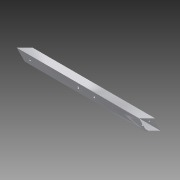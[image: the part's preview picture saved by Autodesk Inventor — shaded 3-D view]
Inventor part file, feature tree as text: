
AUTODESK INVENTOR PART (.ipt)
format: ipt  version: 2015 SP1 (Build 190203100, 203)  size: 176,128 bytes
history: native  units: in
note: dims shown in document units (in); Inventor stores cm internally (conversion verified against a paired STEP export)
features: sketch x7, extrude x4, hole x3, projected_geometry x3
ambient origin geometry x8: Origin, YZ Plane, XZ Plane, XY Plane, X Axis, Y Axis, Z Axis, Center Point
bodies: Solid1 (feature_tree)
feature tree (17):
  extrude  "Extrusion1"  Depth=1.0in
  hole  "Hole1"  [1 undecoded]
  hole  "Hole2"  [1 undecoded]
  hole  "Hole3"  [1 undecoded]
  extrude  "Extrusion2"  Depth=0.5in
  extrude  "Extrusion3"  Depth=1.0in
  extrude  "Extrusion4"  Depth=1.0in
  sketch  "Sketch1"  dims[d0=1.0in d1=1.0in]
  sketch  "Sketch2"  dims[d2=0.75in d3=0.75in]
  projected_geometry  "Projected Loop1"
  sketch  "Sketch3"  dims[d4=0.125in d5=0.125in]
  projected_geometry  "Projected Loop2"
  sketch  "Sketch4"  dims[d6=21.5in d7=0.0in d8=0.5in]
  projected_geometry  "Projected Loop3"
  sketch  "Sketch7"  dims[d9=0.5in d10=0.5in]
  sketch  "Sketch8"  dims[d11=0.5in]
  sketch  "Sketch9"  dims[d12=0.25in d13=0.75in d14=0.375in d15=0.25in d16=0.5635in d17=1.0in d18=0.8108in d19=9.75in d20=9.75in d21=0.5in d22=0.5in d23=0.25in d24=0.75in d25=0.375in d26=0.25in d27=0.5635in d28=1.0in d29=0.8108in d30=1.5in d31=0.5in d32=0.5in d33=1.5in d34=0.1875in d35=0.75in d36=0.375in d37=0.25in d38=0.5635in d39=1.0in d40=0.8108in d65=0.25in d66=0.25in d67=0.5in d68=2.25in d69=0.25in d70=0.25in d71=0.5in d72=2.25in d73=1.0in d74=0.0in d75=1.0in d76=0.0in d77=1.0in d78=0.0in]
note: 3 required parameter values undecoded (feature->parameter linkage not recoverable at this tier; creation-order binding heuristic only, values carry confidence <= 0.55)
